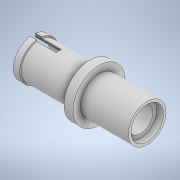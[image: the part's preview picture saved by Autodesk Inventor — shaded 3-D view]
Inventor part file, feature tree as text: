
AUTODESK INVENTOR PART (.ipt)
format: ipt  version: 2020 (Build 240168000, 168)  size: 162,304 bytes
history: native  units: in
note: dims shown in document units (in); Inventor stores cm internally (conversion verified against a paired STEP export)
features: sketch x2, revolve x1, extrude x1
ambient origin geometry x8: Origin, YZ Plane, XZ Plane, XY Plane, X Axis, Y Axis, Z Axis, Center Point
bodies: Solid1 (feature_tree)
feature tree (4):
  revolve  "Revolution1"  [1 undecoded]
  extrude  "Extrusion1"  TaperAngle=90.0deg  [1 undecoded]
  sketch  "Sketch2"  dims[d2=0.095in d4=0.33in]
  sketch  "Sketch3"  dims[d5=0.03in d6=90.0deg d7=0.05in d8=0.02in d9=0.19in d10=0.0in d11=0.03in d12=0.25in d13=0.025in d14=0.05in d15=0.01in d16=360.0deg d17=0.04in d18=0.02in d19=0.2in d20=0.0in]
note: 2 required parameter values undecoded (feature->parameter linkage not recoverable at this tier; creation-order binding heuristic only, values carry confidence <= 0.55)